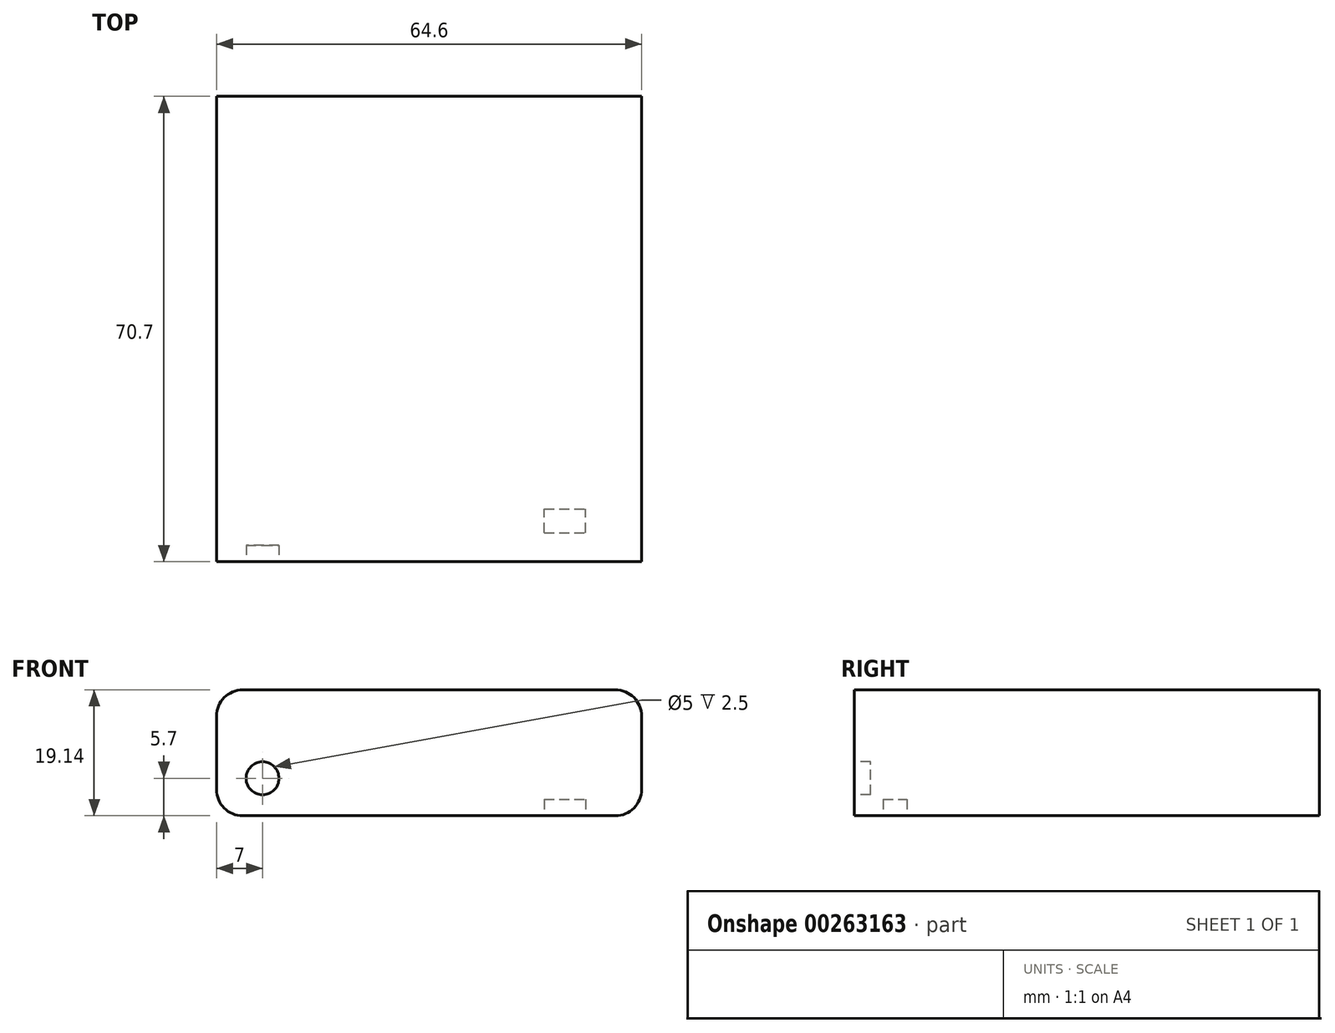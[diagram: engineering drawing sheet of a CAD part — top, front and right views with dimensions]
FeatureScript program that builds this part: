
annotation { "Feature Type Name" : "Feature", "Feature Type Description" : "" }
export const myFeature = defineFeature(function(context is Context, id is Id, definition is map)
    precondition{}
    {
        {
            var Q0;
            Q0=qCreatedBy(makeId("Top.planeOp"),FACE);
            var sketch = newSketch(context, id + "F0", { "sketchPlane" : qUnion([Q0])});
            skLineSegment(sketch, "E0.bottom", {"start": v(-32.3, 35.35) * mm, "end": v(32.3, 35.35) * mm});
            skLineSegment(sketch, "E0.top", {"start": v(-32.3, -35.35) * mm, "end": v(32.3, -35.35) * mm});
            skLineSegment(sketch, "E0.left", {"start": v(-32.3, 35.35) * mm, "end": v(-32.3, -35.35) * mm});
            skLineSegment(sketch, "E0.right", {"start": v(32.3, 35.35) * mm, "end": v(32.3, -35.35) * mm});
            skSolve(sketch);
        }
        {
            var Q0;
            Q0 = qSketchRegion(id + "F0", true);
            extrude(context, id + "F1", {"entities" : qUnion([Q0]), "depth" : 19.14 * mm});
        }
        {
            var Q0;
            Q0=makeQuery(id+"F1.opExtrude","CAP_EDGE",EDGE,{"disambiguationData":[OSD([sQuery(id+"F0.wireOp",EDGE,"E0.left")])],"isStart":false});
            var Q1;
            Q1=makeQuery(id+"F1.opExtrude","CAP_EDGE",EDGE,{"disambiguationData":[OSD([sQuery(id+"F0.wireOp",EDGE,"E0.left")])],"isStart":true});
            var Q2;
            Q2=makeQuery(id+"F1.opExtrude","CAP_EDGE",EDGE,{"disambiguationData":[OSD([sQuery(id+"F0.wireOp",EDGE,"E0.right")])],"isStart":false});
            var Q3;
            Q3=makeQuery(id+"F1.opExtrude","CAP_EDGE",EDGE,{"disambiguationData":[OSD([sQuery(id+"F0.wireOp",EDGE,"E0.right")])],"isStart":true});
            fillet(context, id + "F2", {"entities" : qUnion([Q0, Q1, Q2, Q3]), "radius" : 4 * mm, "tangentPropagation" : true, "allowEdgeOverflow" : false});
        }
        {
            var Q0;
            Q0=makeQuery(id+"F1.opExtrude","SWEPT_FACE",FACE,{"disambiguationData":[OSD([sQuery(id+"F0.wireOp",EDGE,"E0.top")])]});
            var sketch = newSketch(context, id + "F3", { "sketchPlane" : qUnion([Q0])});
            skCircle(sketch, "E1", {"center": v(-25.3, 5.7) * mm, "radius": 2.5 * mm});
            skSolve(sketch);
        }
        {
            var Q0;
            Q0 = qSketchRegion(id + "F3", true);
            extrude(context, id + "F4", {"entities" : qUnion([Q0]), "operationType" : NewBodyOperationType.REMOVE, "oppositeDirection" : true, "depth" : 2.5 * mm});
        }
        {
            var Q0;
            Q0=makeQuery(id+"F1.opExtrude","CAP_FACE",FACE,{"disambiguationData":[OSD([sQuery(id+"F0.wireOp",EDGE,"E0.bottom"),sQuery(id+"F0.wireOp",EDGE,"E0.top"),sQuery(id+"F0.wireOp",EDGE,"E0.left"),sQuery(id+"F0.wireOp",EDGE,"E0.right")])],"isStart":true});
            var sketch = newSketch(context, id + "F5", { "sketchPlane" : qUnion([Q0])});
            skLineSegment(sketch, "E2.bottom", {"start": v(17.5, 30.95) * mm, "end": v(23.8, 30.95) * mm});
            skLineSegment(sketch, "E2.top", {"start": v(17.5, 27.35) * mm, "end": v(23.8, 27.35) * mm});
            skLineSegment(sketch, "E2.left", {"start": v(17.5, 30.95) * mm, "end": v(17.5, 27.35) * mm});
            skLineSegment(sketch, "E2.right", {"start": v(23.8, 30.95) * mm, "end": v(23.8, 27.35) * mm});
            skSolve(sketch);
        }
        {
            var Q0;
            Q0 = qSketchRegion(id + "F5", true);
            extrude(context, id + "F6", {"entities" : qUnion([Q0]), "operationType" : NewBodyOperationType.REMOVE, "oppositeDirection" : true, "depth" : 2.5 * mm});
        }
    });
